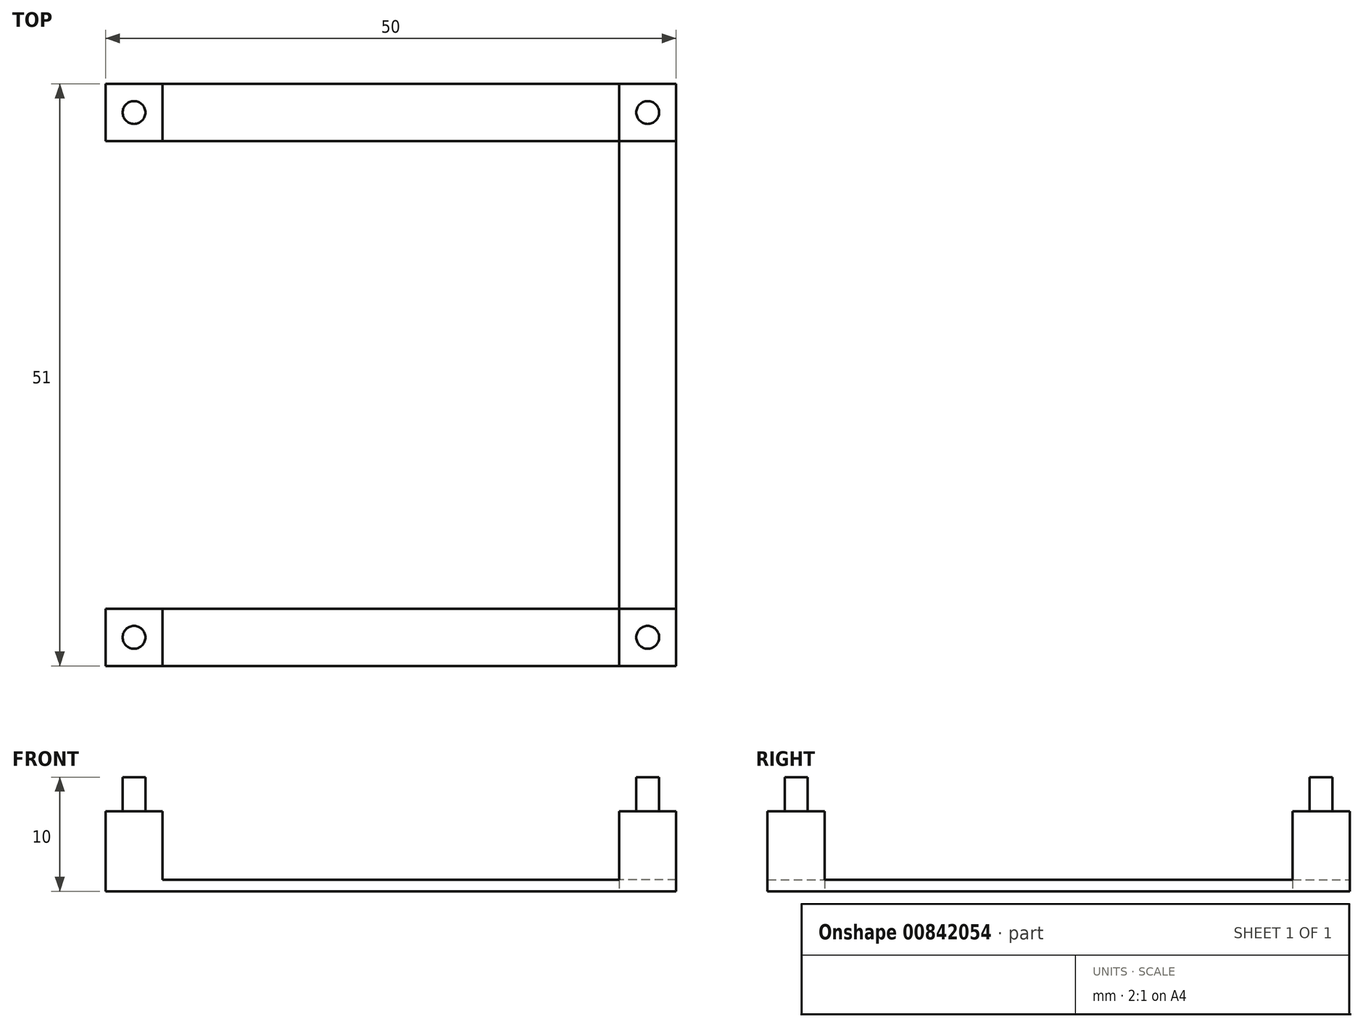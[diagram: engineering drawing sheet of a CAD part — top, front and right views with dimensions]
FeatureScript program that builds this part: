
annotation { "Feature Type Name" : "Feature", "Feature Type Description" : "" }
export const myFeature = defineFeature(function(context is Context, id is Id, definition is map)
    precondition{}
    {
        {
            var Q0;
            Q0=qCreatedBy(makeId("Top.planeOp"),FACE);
            var sketch = newSketch(context, id + "F0", { "sketchPlane" : qUnion([Q0])});
            skLineSegment(sketch, "E0.bottom", {"start": v(25, -25.5) * mm, "end": v(-25, -25.5) * mm});
            skLineSegment(sketch, "E0.top", {"start": v(25, 25.5) * mm, "end": v(-25, 25.5) * mm});
            skLineSegment(sketch, "E0.left", {"start": v(25, -25.5) * mm, "end": v(25, 25.5) * mm});
            skLineSegment(sketch, "E0.right", {"start": v(-25, -25.5) * mm, "end": v(-25, 25.5) * mm});
            skPoint(sketch, "E0.middle", {"position": v(0, 0) * mm});
            skLineSegment(sketch, "E1.bottom", {"start": v(-25, -25.5) * mm, "end": v(25, -25.5) * mm});
            skLineSegment(sketch, "E1.top", {"start": v(-25, -20.5) * mm, "end": v(25, -20.5) * mm});
            skLineSegment(sketch, "E1.left", {"start": v(-25, -25.5) * mm, "end": v(-25, -20.5) * mm});
            skLineSegment(sketch, "E1.right", {"start": v(25, -25.5) * mm, "end": v(25, -20.5) * mm});
            skLineSegment(sketch, "E2.bottom", {"start": v(-25, 20.5) * mm, "end": v(25, 20.5) * mm});
            skLineSegment(sketch, "E2.top", {"start": v(-25, 25.5) * mm, "end": v(25, 25.5) * mm});
            skLineSegment(sketch, "E2.left", {"start": v(-25, 20.5) * mm, "end": v(-25, 25.5) * mm});
            skLineSegment(sketch, "E2.right", {"start": v(25, 20.5) * mm, "end": v(25, 25.5) * mm});
            skLineSegment(sketch, "E3.bottom", {"start": v(-25, 25.5) * mm, "end": v(-20, 25.5) * mm});
            skLineSegment(sketch, "E3.top", {"start": v(-25, 20.5) * mm, "end": v(-20, 20.5) * mm});
            skLineSegment(sketch, "E3.left", {"start": v(-25, 25.5) * mm, "end": v(-25, 20.5) * mm});
            skLineSegment(sketch, "E3.right", {"start": v(-20, 25.5) * mm, "end": v(-20, 20.5) * mm});
            skLineSegment(sketch, "E4.bottom", {"start": v(25, 25.5) * mm, "end": v(20, 25.5) * mm});
            skLineSegment(sketch, "E4.top", {"start": v(25, 20.5) * mm, "end": v(20, 20.5) * mm});
            skLineSegment(sketch, "E4.left", {"start": v(25, 25.5) * mm, "end": v(25, 20.5) * mm});
            skLineSegment(sketch, "E4.right", {"start": v(20, 25.5) * mm, "end": v(20, 20.5) * mm});
            skLineSegment(sketch, "E5.bottom", {"start": v(25, -20.5) * mm, "end": v(20, -20.5) * mm});
            skLineSegment(sketch, "E5.top", {"start": v(25, -25.5) * mm, "end": v(20, -25.5) * mm});
            skLineSegment(sketch, "E5.left", {"start": v(25, -20.5) * mm, "end": v(25, -25.5) * mm});
            skLineSegment(sketch, "E5.right", {"start": v(20, -20.5) * mm, "end": v(20, -25.5) * mm});
            skLineSegment(sketch, "E6.bottom", {"start": v(-25, -20.5) * mm, "end": v(-20, -20.5) * mm});
            skLineSegment(sketch, "E6.top", {"start": v(-25, -25.5) * mm, "end": v(-20, -25.5) * mm});
            skLineSegment(sketch, "E6.left", {"start": v(-25, -20.5) * mm, "end": v(-25, -25.5) * mm});
            skLineSegment(sketch, "E6.right", {"start": v(-20, -20.5) * mm, "end": v(-20, -25.5) * mm});
            skCircle(sketch, "E7", {"center": v(-22.5, 23) * mm, "radius": 1 * mm});
            skPoint(sketch, "E7.centerSnap0", {"position": v(-25, 23) * mm});
            skPoint(sketch, "E7.centerSnap1", {"position": v(-22.5, 20.5) * mm});
            skCircle(sketch, "E8", {"center": v(22.5, 23) * mm, "radius": 1 * mm});
            skPoint(sketch, "E8.centerSnap0", {"position": v(22.5, 20.5) * mm});
            skPoint(sketch, "E8.centerSnap1", {"position": v(20, 23) * mm});
            skCircle(sketch, "E9", {"center": v(22.5, -23) * mm, "radius": 1 * mm});
            skPoint(sketch, "E9.centerSnap0", {"position": v(22.5, -25.5) * mm});
            skPoint(sketch, "E9.centerSnap1", {"position": v(20, -23) * mm});
            skCircle(sketch, "E10", {"center": v(-22.5, -23) * mm, "radius": 1 * mm});
            skPoint(sketch, "E10.centerSnap0", {"position": v(-22.5, -25.5) * mm});
            skPoint(sketch, "E10.centerSnap1", {"position": v(-25, -23) * mm});
            skLineSegment(sketch, "E11.bottom", {"start": v(20, 20.5) * mm, "end": v(25, 20.5) * mm});
            skLineSegment(sketch, "E11.top", {"start": v(20, -20.5) * mm, "end": v(25, -20.5) * mm});
            skLineSegment(sketch, "E11.left", {"start": v(20, 20.5) * mm, "end": v(20, -20.5) * mm});
            skLineSegment(sketch, "E11.right", {"start": v(25, 20.5) * mm, "end": v(25, -20.5) * mm});
            skSolve(sketch);
        }
        {
            var Q0;
            {var subQ0=sQuery(id+"F0.wireOp",EDGE,"E5.right");Q0=makeQuery(id+"F0.imprint","IMPRINT",FACE,{"disambiguationData":[TD([[makeQuery(id+"F0.imprint","IMPRINT",EDGE,{"derivedFrom":subQ0}),-1.0]])]});}
            var Q1;
            {var subQ2=sQuery(id+"F0.wireOp",EDGE,"E3.right");Q1=makeQuery(id+"F0.imprint","IMPRINT",FACE,{"disambiguationData":[TD([[makeQuery(id+"F0.imprint","IMPRINT",EDGE,{"derivedFrom":subQ2}),1.0]])]});}
            var Q2;
            {var subQ0=sQuery(id+"F0.wireOp",EDGE,"E3.right");Q2=makeQuery(id+"F0.imprint","IMPRINT",FACE,{"disambiguationData":[TD([[makeQuery(id+"F0.imprint","IMPRINT",EDGE,{"derivedFrom":subQ0}),-1.0]])]});}
            var Q3;
            {var subQ0=sQuery(id+"F0.wireOp",EDGE,"E4.right");Q3=makeQuery(id+"F0.imprint","IMPRINT",FACE,{"disambiguationData":[TD([[makeQuery(id+"F0.imprint","IMPRINT",EDGE,{"derivedFrom":subQ0}),1.0]])]});}
            var Q4;
            {var subQ0=sQuery(id+"F0.wireOp",EDGE,"E5.right");Q4=makeQuery(id+"F0.imprint","IMPRINT",FACE,{"disambiguationData":[TD([[makeQuery(id+"F0.imprint","IMPRINT",EDGE,{"derivedFrom":subQ0}),1.0]])]});}
            var Q5;
            {var subQ3=sQuery(id+"F0.wireOp",EDGE,"E6.right");Q5=makeQuery(id+"F0.imprint","IMPRINT",FACE,{"disambiguationData":[TD([[makeQuery(id+"F0.imprint","IMPRINT",EDGE,{"derivedFrom":subQ3}),-1.0]])]});}
            var Q6;
            {var subQ5=sQuery(id+"F0.wireOp",EDGE,"E11.left");Q6=makeQuery(id+"F0.imprint","IMPRINT",FACE,{"disambiguationData":[TD([[makeQuery(id+"F0.imprint","IMPRINT",EDGE,{"derivedFrom":subQ5}),1.0]])]});}
            var Q7;
            Q7=makeQuery(id+"F0.imprint","IMPRINT",FACE,{"disambiguationData":[TD([[makeQuery(id+"F0.imprint","IMPRINT",EDGE,{"derivedFrom":sQuery(id+"F0.wireOp",EDGE,"E7")}),1.0]])]});
            var Q8;
            Q8=makeQuery(id+"F0.imprint","IMPRINT",FACE,{"disambiguationData":[TD([[makeQuery(id+"F0.imprint","IMPRINT",EDGE,{"derivedFrom":sQuery(id+"F0.wireOp",EDGE,"E8")}),1.0]])]});
            var Q9;
            Q9=makeQuery(id+"F0.imprint","IMPRINT",FACE,{"disambiguationData":[TD([[makeQuery(id+"F0.imprint","IMPRINT",EDGE,{"derivedFrom":sQuery(id+"F0.wireOp",EDGE,"E9")}),1.0]])]});
            var Q10;
            Q10=makeQuery(id+"F0.imprint","IMPRINT",FACE,{"disambiguationData":[TD([[makeQuery(id+"F0.imprint","IMPRINT",EDGE,{"derivedFrom":sQuery(id+"F0.wireOp",EDGE,"E10")}),1.0]])]});
            extrude(context, id + "F1", {"entities" : qUnion([Q0, Q1, Q2, Q3, Q4, Q5, Q6, Q7, Q8, Q9, Q10]), "depth" : 1 * mm, "offsetDistance" : 25 * mm});
        }
        {
            var Q0;
            {var subQ0=sQuery(id+"F0.wireOp",EDGE,"E4.right");Q0=makeQuery(id+"F0.imprint","IMPRINT",FACE,{"disambiguationData":[TD([[makeQuery(id+"F0.imprint","IMPRINT",EDGE,{"derivedFrom":subQ0}),1.0]])]});}
            var Q1;
            Q1=makeQuery(id+"F0.imprint","IMPRINT",FACE,{"disambiguationData":[TD([[makeQuery(id+"F0.imprint","IMPRINT",EDGE,{"derivedFrom":sQuery(id+"F0.wireOp",EDGE,"E8")}),1.0]])]});
            var Q2;
            {var subQ0=sQuery(id+"F0.wireOp",EDGE,"E3.right");Q2=makeQuery(id+"F0.imprint","IMPRINT",FACE,{"disambiguationData":[TD([[makeQuery(id+"F0.imprint","IMPRINT",EDGE,{"derivedFrom":subQ0}),-1.0]])]});}
            var Q3;
            Q3=makeQuery(id+"F0.imprint","IMPRINT",FACE,{"disambiguationData":[TD([[makeQuery(id+"F0.imprint","IMPRINT",EDGE,{"derivedFrom":sQuery(id+"F0.wireOp",EDGE,"E7")}),1.0]])]});
            var Q4;
            {var subQ0=sQuery(id+"F0.wireOp",EDGE,"E5.right");Q4=makeQuery(id+"F0.imprint","IMPRINT",FACE,{"disambiguationData":[TD([[makeQuery(id+"F0.imprint","IMPRINT",EDGE,{"derivedFrom":subQ0}),1.0]])]});}
            var Q5;
            Q5=makeQuery(id+"F0.imprint","IMPRINT",FACE,{"disambiguationData":[TD([[makeQuery(id+"F0.imprint","IMPRINT",EDGE,{"derivedFrom":sQuery(id+"F0.wireOp",EDGE,"E9")}),1.0]])]});
            var Q6;
            {var subQ3=sQuery(id+"F0.wireOp",EDGE,"E6.right");Q6=makeQuery(id+"F0.imprint","IMPRINT",FACE,{"disambiguationData":[TD([[makeQuery(id+"F0.imprint","IMPRINT",EDGE,{"derivedFrom":subQ3}),-1.0]])]});}
            var Q7;
            Q7=makeQuery(id+"F0.imprint","IMPRINT",FACE,{"disambiguationData":[TD([[makeQuery(id+"F0.imprint","IMPRINT",EDGE,{"derivedFrom":sQuery(id+"F0.wireOp",EDGE,"E10")}),1.0]])]});
            extrude(context, id + "F2", {"entities" : qUnion([Q0, Q1, Q2, Q3, Q4, Q5, Q6, Q7]), "operationType" : NewBodyOperationType.ADD, "depth" : 7 * mm, "offsetDistance" : 25 * mm});
        }
        {
            var Q0;
            Q0=makeQuery(id+"F0.imprint","IMPRINT",FACE,{"disambiguationData":[TD([[makeQuery(id+"F0.imprint","IMPRINT",EDGE,{"derivedFrom":sQuery(id+"F0.wireOp",EDGE,"E8")}),1.0]])]});
            var Q1;
            Q1=makeQuery(id+"F0.imprint","IMPRINT",FACE,{"disambiguationData":[TD([[makeQuery(id+"F0.imprint","IMPRINT",EDGE,{"derivedFrom":sQuery(id+"F0.wireOp",EDGE,"E7")}),1.0]])]});
            var Q2;
            Q2=makeQuery(id+"F0.imprint","IMPRINT",FACE,{"disambiguationData":[TD([[makeQuery(id+"F0.imprint","IMPRINT",EDGE,{"derivedFrom":sQuery(id+"F0.wireOp",EDGE,"E10")}),1.0]])]});
            var Q3;
            Q3=makeQuery(id+"F0.imprint","IMPRINT",FACE,{"disambiguationData":[TD([[makeQuery(id+"F0.imprint","IMPRINT",EDGE,{"derivedFrom":sQuery(id+"F0.wireOp",EDGE,"E9")}),1.0]])]});
            extrude(context, id + "F3", {"entities" : qUnion([Q0, Q1, Q2, Q3]), "operationType" : NewBodyOperationType.ADD, "depth" : 10 * mm, "offsetDistance" : 25 * mm});
        }
    });
